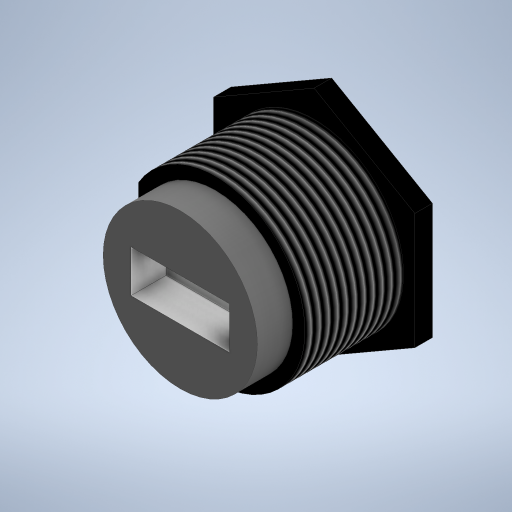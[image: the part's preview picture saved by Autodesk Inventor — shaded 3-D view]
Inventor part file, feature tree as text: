
AUTODESK INVENTOR PART (.ipt)
format: ipt  version: 2023 (Build 270158000, 158)  size: 315,904 bytes
history: native  units: in
note: dims shown in document units (in); Inventor stores cm internally (conversion verified against a paired STEP export)
features: extrude x4, sketch x4, thread x1
ambient origin geometry x8: Origin, YZ Plane, XZ Plane, XY Plane, X Axis, Y Axis, Z Axis, Center Point
bodies: Solid1 (feature_tree)
feature tree (9):
  extrude  "Extrusion1"  Depth=0.9311in
  extrude  "Extrusion2"  Depth=1.126in
  extrude  "Extrusion3"  Depth=0.1969in TaperAngle=0.0deg
  extrude  "Extrusion4"  Depth=0.2362in
  thread  "Thread1"  [1 undecoded]
  sketch  "Sketch1"  dims[d0=1.0in d1=0.9311in]
  sketch  "Sketch2"  dims[d2=0.748in d3=0.0in d5=1.126in]
  sketch  "Sketch3"  dims[d6=0.0984in d7=0.0in d8=0.1969in d9=0.0in]
  sketch  "Sketch4"  dims[d10=0.5512in d11=0.2362in d12=0.1969in d13=0.0in d14=0.5512in d15=0.0in]
note: 1 required parameter value undecoded (feature->parameter linkage not recoverable at this tier; creation-order binding heuristic only, values carry confidence <= 0.55)
